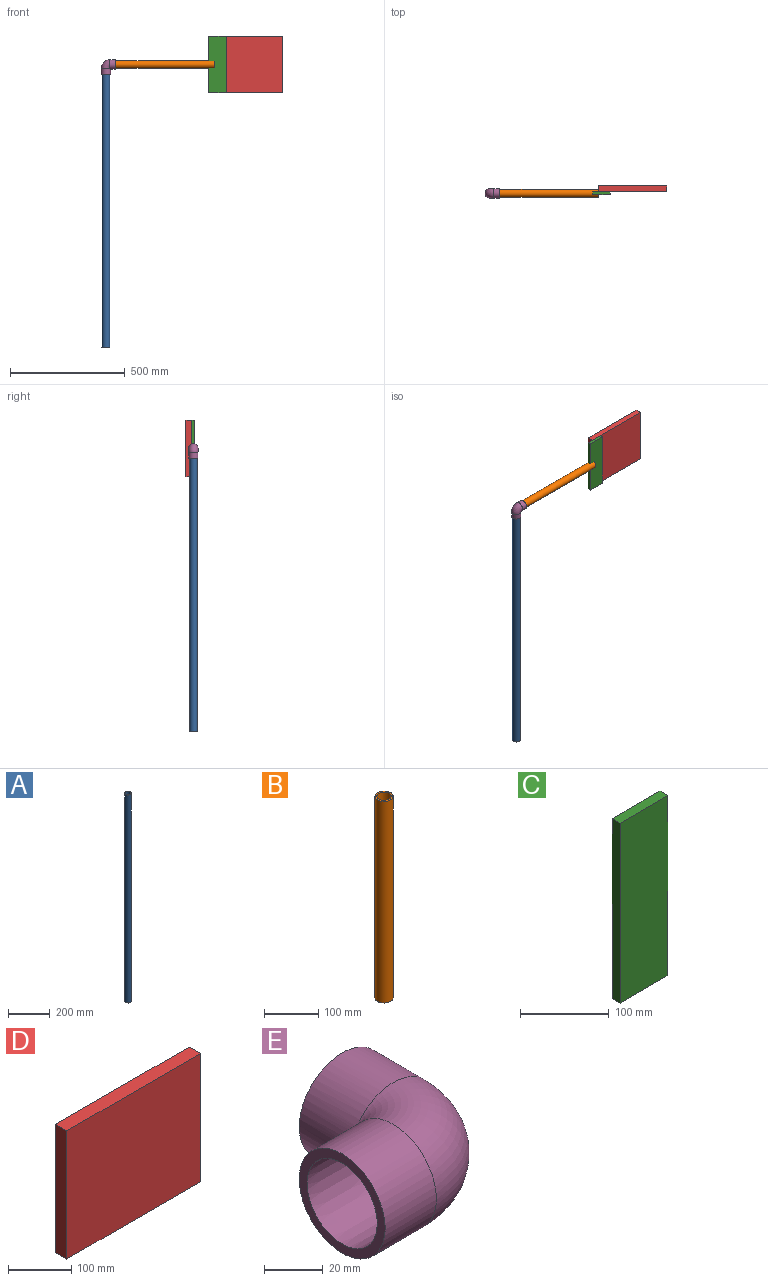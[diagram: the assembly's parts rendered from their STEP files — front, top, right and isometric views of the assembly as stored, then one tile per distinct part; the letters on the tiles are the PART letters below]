
ASSEMBLY  parts=5 mates=7
PART A: 4 faces, bbox 33.4x33.4x1219.2 mm
  f0: cylinder r=13.32mm len=1219.2mm, axis (0,0,-1), area 102054.9mm2, adj f2,f3
  f1: cylinder r=16.7mm len=1219.2mm, axis (0,0,-1), area 127933.5mm2, adj f2,f3
  f2: plane 33.4x33.4mm, normal (0,0,1), area 318.6mm2, adj f0,f1
  f3: plane 33.4x33.4mm, normal (0,0,-1), area 318.6mm2, adj f0,f1
PART B: 4 faces, bbox 33.4x33.4x457.2 mm
  f0: cylinder r=13.32mm len=457.2mm, axis (0,0,-1), area 38270.6mm2, adj f2,f3
  f1: cylinder r=16.7mm len=457.2mm, axis (0,0,-1), area 47975.1mm2, adj f2,f3
  f2: plane 33.4x33.4mm, normal (0,0,1), area 318.6mm2, adj f0,f1
  f3: plane 33.4x33.4mm, normal (0,0,-1), area 318.6mm2, adj f0,f1
PART C: 6 faces, bbox 76.2x12.7x247.7 mm
  f0: plane 76.2x12.7mm, normal (0,0,-1), area 967.7mm2, adj f1,f3,f4,f5
  f1: plane 247.65x12.7mm, normal (1,0,0), area 3145.2mm2, adj f0,f2,f4,f5
  f2: plane 76.2x12.7mm, normal (0,0,1), area 967.7mm2, adj f1,f3,f4,f5
  f3: plane 247.65x12.7mm, normal (-1,0,0), area 3145.2mm2, adj f0,f2,f4,f5
  f4: plane 247.65x76.2mm, normal (0,-1,0), area 18870.9mm2, adj f0,f1,f2,f3
  f5: plane 247.65x76.2mm, normal (0,1,0), area 18870.9mm2, adj f0,f1,f2,f3
PART D: 6 faces, bbox 298.5x25.4x247.7 mm
  f0: plane 298.45x25.4mm, normal (0,0,-1), area 7580.6mm2, adj f1,f3,f4,f5
  f1: plane 247.65x25.4mm, normal (1,0,0), area 6290.3mm2, adj f0,f2,f4,f5
  f2: plane 298.45x25.4mm, normal (0,0,1), area 7580.6mm2, adj f1,f3,f4,f5
  f3: plane 247.65x25.4mm, normal (-1,0,0), area 6290.3mm2, adj f0,f2,f4,f5
  f4: plane 298.45x247.65mm, normal (0,-1,0), area 73911.1mm2, adj f0,f1,f2,f3
  f5: plane 298.45x247.65mm, normal (0,1,0), area 73911.1mm2, adj f0,f1,f2,f3
PART E: 10 faces, bbox 62.7x62.7x41.3 mm
  f0: plane 41.28x41.28mm, normal (-1,0,0), area 448.4mm2, adj f1,f2
  f1: cone r=16.64mm half-angle=0.4deg, axis (-1,0,0), area 2587mm2, adj f0,f6
  f2: cylinder r=20.64mm len=41.28mm, axis (-1,0,0), area 3141.8mm2, adj f0,f4,f8
  f3: torus R=17.46mm, axis (0,0,-1), area 2296.1mm2, adj f5,f6
  f4: torus R=17.46mm, axis (0,0,-1), area 3633.6mm2, adj f2,f8
  f5: plane 33.27x33.27mm, normal (0,1,0), area 312mm2, adj f3,f9
  f6: plane 33.27x33.27mm, normal (-1,0,0), area 312mm2, adj f1,f3
  f7: plane 41.28x41.28mm, normal (0,1,0), area 448.4mm2, adj f8,f9
  f8: cylinder r=20.64mm len=41.28mm, axis (0,-1,0), area 3141.8mm2, adj f2,f4,f7
  f9: cone r=16.83mm half-angle=0.4deg, axis (0,1,0), area 2587mm2, adj f5,f7
PLACE A rot(axis=(0.01,0.01,1),0deg) t=(-246.06,0,-627.06)mm
PLACE B rot(axis=(0.58,-0.58,-0.58),120deg) t=(0,0,0)mm fixed
PLACE C rot(axis=(0,1,0),180deg) t=(241.3,0,0)mm
PLACE D rot(axis=(-0.02,-1,0),0deg) t=(377.82,19.05,0)mm
PLACE E rot(axis=(0,0.71,-0.71),180deg) t=(-246.06,0,0)mm
MATE fastened E.f1 <-> B.f0  axis (1,0,0) through (-228.6,0,0)mm
MATE planar B.f1 <-> D.f3  axis (1,0,0) through (228.6,0,0)mm
MATE planar D.f2 <-> C.f0  axis (0,0,1) through (377.82,19.05,123.83)mm
MATE planar C.f3 <-> B.f0  axis (1,0,0) through (279.4,0,0)mm
MATE planar D.f4 <-> C.f5  axis (0,-1,0) through (377.82,6.35,0)mm
MATE slider B.f1 <-> C.f1  axis (1,0,0) through (228.6,0,0)mm
MATE fastened E.f8 <-> A.f0  axis (0,0,-1) through (-246.06,0,-17.46)mm
